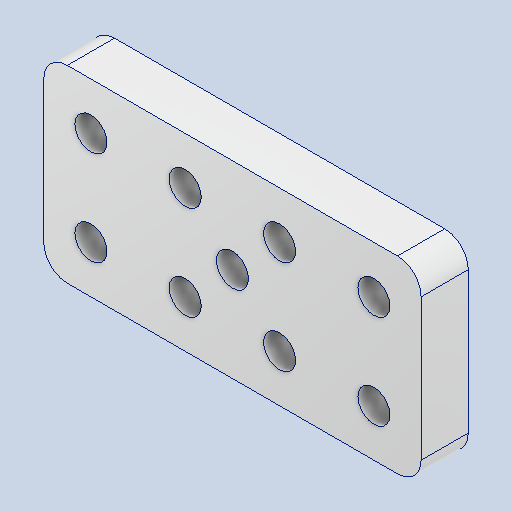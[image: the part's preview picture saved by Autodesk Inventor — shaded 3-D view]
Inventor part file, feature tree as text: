
AUTODESK INVENTOR PART (.ipt)
format: ipt  version: 2023 (Build 270158000, 158)  size: 267,264 bytes
history: native  units: in
note: dims shown in document units (in); Inventor stores cm internally (conversion verified against a paired STEP export)
features: extrude x1, fillet x1, sketch x1
ambient origin geometry x8: Origin, YZ Plane, XZ Plane, XY Plane, X Axis, Y Axis, Z Axis, Center Point
bodies: Solid1 (feature_tree)
feature tree (3):
  extrude  "Extrusion1"  Depth=1.5in
  fillet  "Fillet1"  Radius=0.5in
  sketch  "Sketch1"  dims[d0=0.17in d1=1.5in d9=0.5in d10=1.5748in d12=0.5in d13=0.7874in d15=0.5in d18=0.17in d19=1.0in d20=0.25in d21=0.0in d22=0.125in]
